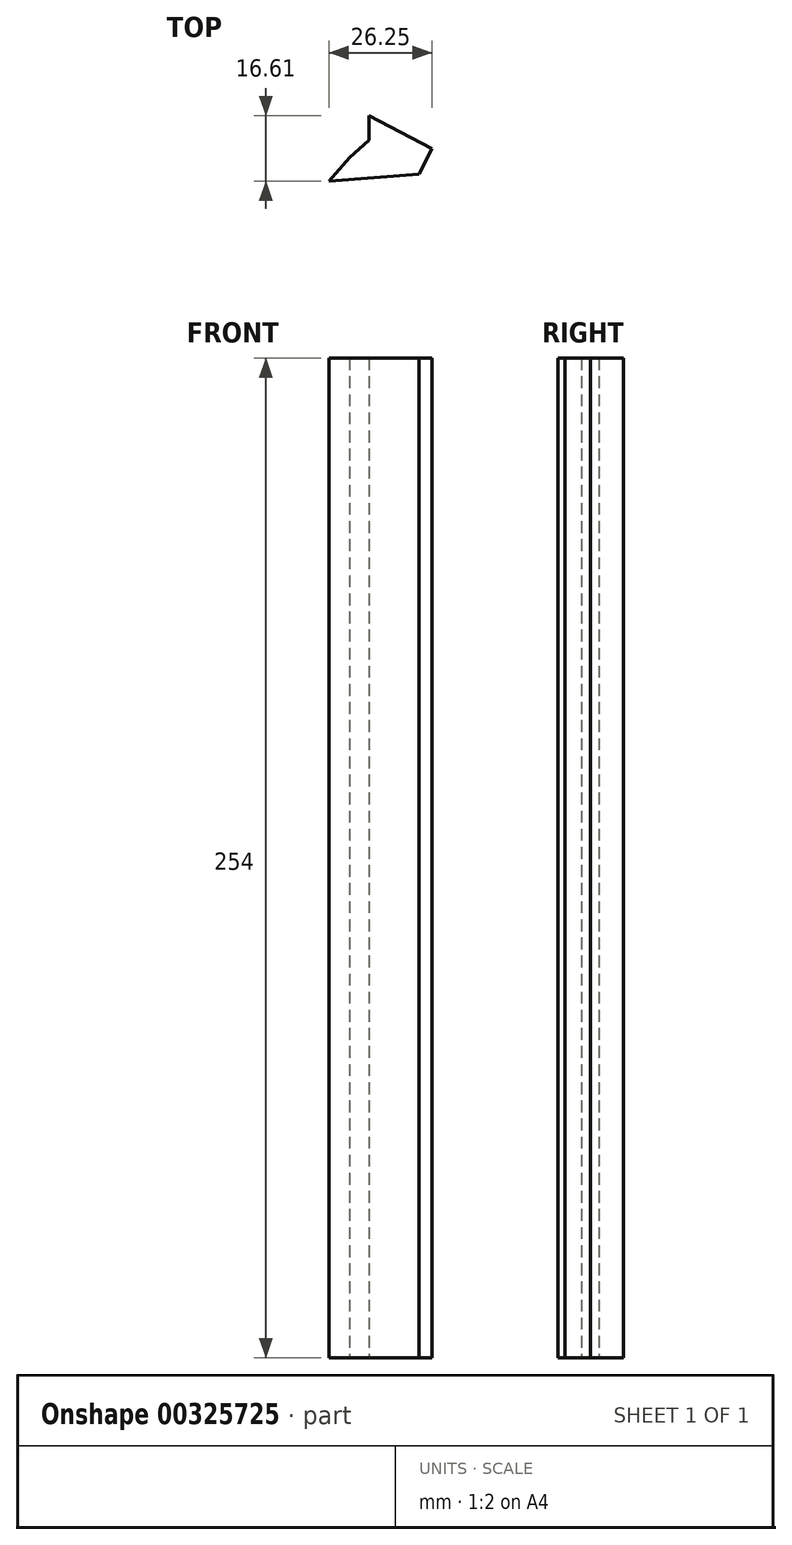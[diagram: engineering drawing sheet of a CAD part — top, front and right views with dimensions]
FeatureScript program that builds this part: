
annotation { "Feature Type Name" : "Feature", "Feature Type Description" : "" }
export const myFeature = defineFeature(function(context is Context, id is Id, definition is map)
    precondition{}
    {
        {
            var Q0;
            Q0=qCreatedBy(makeId("Top.planeOp"),FACE);
            var sketch = newSketch(context, id + "F0", { "sketchPlane" : qUnion([Q0])});
            skLineSegment(sketch, "E0", {"start": v(0, 0) * mm, "end": v(22.86, 1.76) * mm});
            skLineSegment(sketch, "E1", {"start": v(22.86, 1.76) * mm, "end": v(26.25, 8.26) * mm});
            skLineSegment(sketch, "E2", {"start": v(26.25, 8.26) * mm, "end": v(10.24, 16.6) * mm});
            skLineSegment(sketch, "E3", {"start": v(10.24, 16.6) * mm, "end": v(10.24, 10.37) * mm});
            skLineSegment(sketch, "E4", {"start": v(10.24, 10.37) * mm, "end": v(5.22, 6) * mm});
            skLineSegment(sketch, "E5", {"start": v(5.22, 6) * mm, "end": v(0, 0) * mm});
            skSolve(sketch);
        }
        {
            var Q0;
            Q0=makeQuery(id+"F0.imprint","IMPRINT",FACE,{"disambiguationData":[TD([[makeQuery(id+"F0.imprint","IMPRINT",EDGE,{"derivedFrom":sQuery(id+"F0.wireOp",EDGE,"E0")}),1.0]])]});
            extrude(context, id + "F1", {"entities" : qUnion([Q0]), "depth" : 254 * mm, "offsetDistance" : 25.4 * mm});
        }
    });
